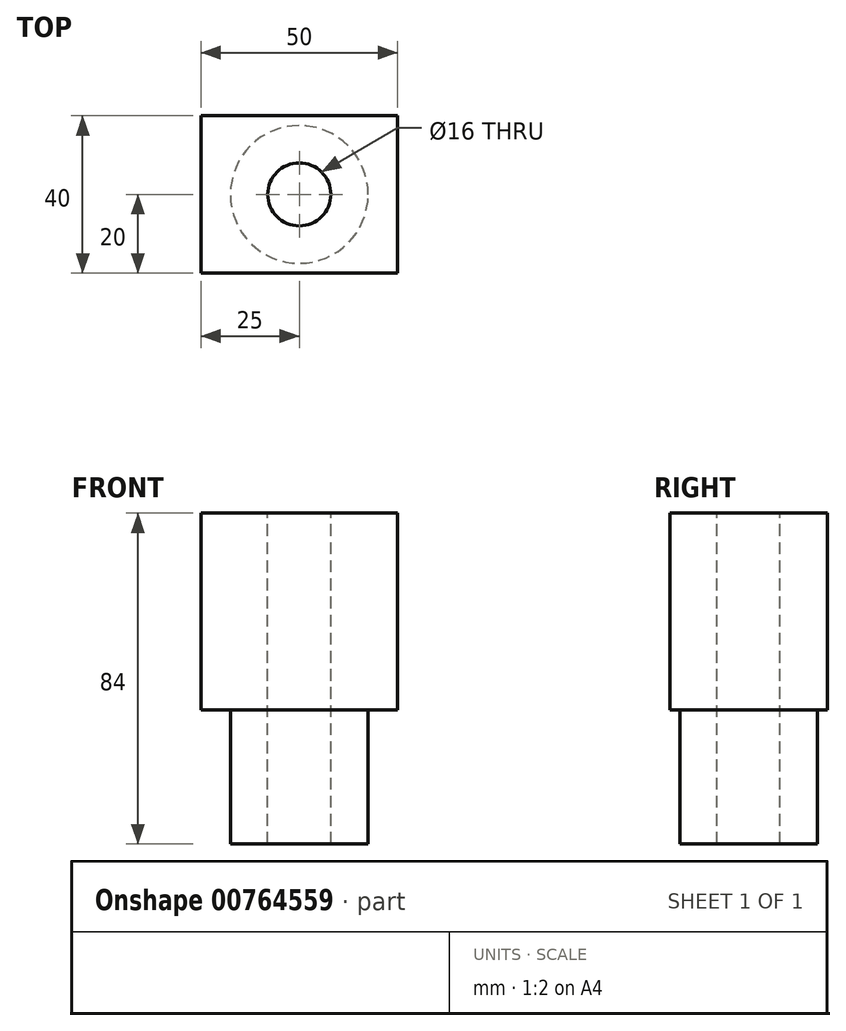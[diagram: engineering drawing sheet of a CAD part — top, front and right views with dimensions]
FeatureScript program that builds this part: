
annotation { "Feature Type Name" : "Feature", "Feature Type Description" : "" }
export const myFeature = defineFeature(function(context is Context, id is Id, definition is map)
    precondition{}
    {
        {
            var Q0;
            Q0=qCreatedBy(makeId("Top.planeOp"),FACE);
            var sketch = newSketch(context, id + "F0", { "sketchPlane" : qUnion([Q0])});
            skLineSegment(sketch, "E0.bottom", {"start": v(25, 20) * mm, "end": v(-25, 20) * mm});
            skLineSegment(sketch, "E0.top", {"start": v(25, -20) * mm, "end": v(-25, -20) * mm});
            skLineSegment(sketch, "E0.left", {"start": v(25, 20) * mm, "end": v(25, -20) * mm});
            skLineSegment(sketch, "E0.right", {"start": v(-25, 20) * mm, "end": v(-25, -20) * mm});
            skPoint(sketch, "E0.middle", {"position": v(0, 0) * mm});
            skSolve(sketch);
        }
        {
            var Q0;
            Q0=makeQuery(id+"F0.imprint","IMPRINT",FACE,{"disambiguationData":[TD([[makeQuery(id+"F0.imprint","IMPRINT",EDGE,{"derivedFrom":sQuery(id+"F0.wireOp",EDGE,"E0.bottom")}),1.0]])]});
            extrude(context, id + "F1", {"entities" : qUnion([Q0]), "depth" : 50 * mm, "offsetDistance" : 25 * mm});
        }
        {
            var Q0;
            Q0=makeQuery(id+"F1.opExtrude","CAP_FACE",FACE,{"disambiguationData":[OSD([sQuery(id+"F0.wireOp",EDGE,"E0.bottom"),sQuery(id+"F0.wireOp",EDGE,"E0.top"),sQuery(id+"F0.wireOp",EDGE,"E0.left"),sQuery(id+"F0.wireOp",EDGE,"E0.right")])],"isStart":true});
            var sketch = newSketch(context, id + "F2", { "sketchPlane" : qUnion([Q0])});
            skCircle(sketch, "E1", {"center": v(0, 0) * mm, "radius": 17.5 * mm});
            skSolve(sketch);
        }
        {
            var Q0;
            Q0=makeQuery(id+"F2.imprint","IMPRINT",FACE,{"disambiguationData":[TD([[makeQuery(id+"F2.imprint","IMPRINT",EDGE,{"derivedFrom":sQuery(id+"F2.wireOp",EDGE,"E1")}),1.0]])]});
            extrude(context, id + "F3", {"entities" : qUnion([Q0]), "operationType" : NewBodyOperationType.ADD, "depth" : 34 * mm, "offsetDistance" : 25 * mm});
        }
        {
            var Q0;
            Q0=makeQuery(id+"F1.opExtrude","CAP_FACE",FACE,{"disambiguationData":[OSD([sQuery(id+"F0.wireOp",EDGE,"E0.bottom"),sQuery(id+"F0.wireOp",EDGE,"E0.top"),sQuery(id+"F0.wireOp",EDGE,"E0.left"),sQuery(id+"F0.wireOp",EDGE,"E0.right")])],"isStart":false});
            var sketch = newSketch(context, id + "F4", { "sketchPlane" : qUnion([Q0])});
            skPoint(sketch, "E2", {"position": v(0, 0) * mm});
            skCircle(sketch, "E3", {"center": v(0, 0) * mm, "radius": 8 * mm});
            skSolve(sketch);
        }
        {
            var Q0;
            Q0=makeQuery(id+"F4.imprint","IMPRINT",FACE,{"disambiguationData":[TD([[makeQuery(id+"F4.imprint","IMPRINT",EDGE,{"derivedFrom":sQuery(id+"F4.wireOp",EDGE,"E3")}),1.0]])]});
            extrude(context, id + "F5", {"entities" : qUnion([Q0]), "operationType" : NewBodyOperationType.REMOVE, "endBound" : BoundingType.THROUGH_ALL, "oppositeDirection" : true, "depth" : 25 * mm, "offsetDistance" : 25 * mm});
        }
    });
